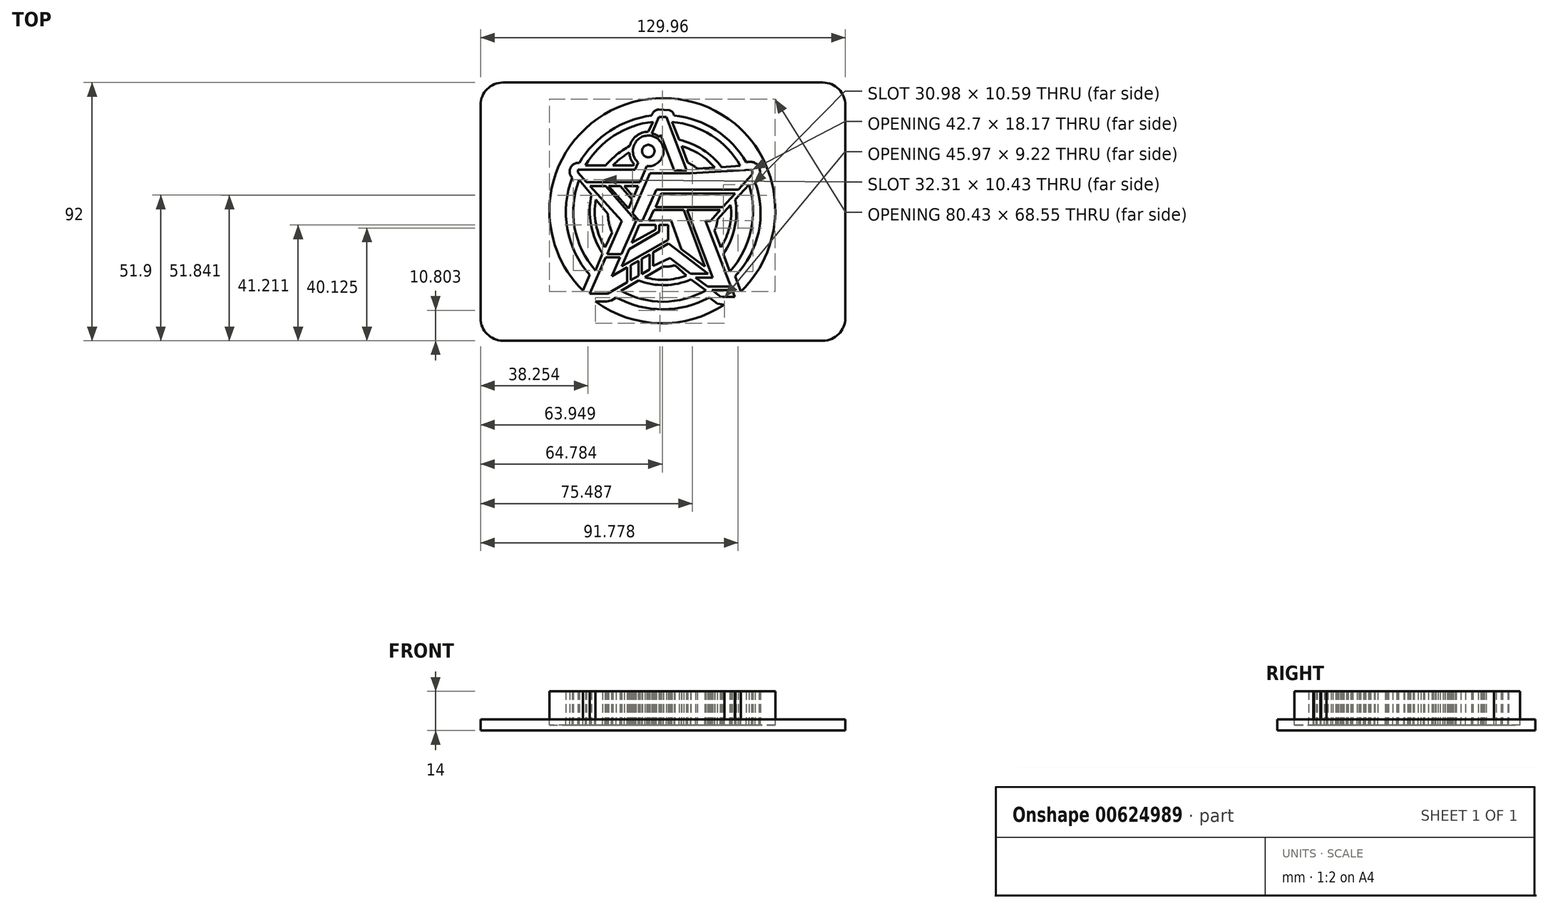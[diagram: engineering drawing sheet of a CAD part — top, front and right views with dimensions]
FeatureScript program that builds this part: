
annotation { "Feature Type Name" : "Feature", "Feature Type Description" : "" }
export const myFeature = defineFeature(function(context is Context, id is Id, definition is map)
    precondition{}
    {
        {
            var Q0;
            Q0=qCreatedBy(makeId("Top.planeOp"),FACE);
            var sketch = newSketch(context, id + "F0", { "sketchPlane" : qUnion([Q0])});
            skCircle(sketch, "E0", {"center": v(0, 0) * mm, "radius": 19.62 * mm, "construction": true});
            skCircle(sketch, "E1", {"center": v(0, 0) * mm, "radius": 24.24 * mm, "construction": true});
            skCircle(sketch, "E2", {"center": v(0, 0) * mm, "radius": 34.5 * mm, "construction": true});
            skLineSegment(sketch, "E3", {"start": v(20.7, -30.4) * mm, "end": v(2.49, -16.49) * mm, "construction": true});
            skLineSegment(sketch, "E4", {"start": v(2.49, -16.49) * mm, "end": v(-19.72, -29.2) * mm, "construction": true});
            skLineSegment(sketch, "E5", {"start": v(2, -11.38) * mm, "end": v(-18.24, -22.97) * mm, "construction": true});
            skLineSegment(sketch, "E6", {"start": v(-18.24, -22.97) * mm, "end": v(-9.56, -3.39) * mm, "construction": true});
            skLineSegment(sketch, "E7", {"start": v(-5.7, 16.2) * mm, "end": v(-12.28, 1.1) * mm, "construction": true});
            skLineSegment(sketch, "E8", {"start": v(-25.9, 9.11) * mm, "end": v(-8.79, 9.11) * mm, "construction": true});
            skLineSegment(sketch, "E9", {"start": v(23.83, -21.37) * mm, "end": v(18.4, -6.8) * mm, "construction": true});
            skLineSegment(sketch, "E10", {"start": v(30.66, 9.62) * mm, "end": v(19.42, -2.8) * mm, "construction": true});
            skLineSegment(sketch, "E11", {"start": v(25.58, -30.36) * mm, "end": v(15.19, -3.34) * mm, "construction": true});
            skLineSegment(sketch, "E12", {"start": v(15.19, -3.34) * mm, "end": v(16.91, -3.34) * mm, "construction": true});
            skLineSegment(sketch, "E13", {"start": v(16.91, -3.34) * mm, "end": v(31.66, 13.12) * mm, "construction": true});
            skLineSegment(sketch, "E14", {"start": v(27.56, 16.32) * mm, "end": v(12.3, 15.29) * mm, "construction": true});
            skLineSegment(sketch, "E15", {"start": v(3.31, 32) * mm, "end": v(8.9, 17.49) * mm, "construction": true});
            skArc(sketch, "E16", {"start": v(12.3, 15.29) * mm, "mid": v(10.66, 16.48) * mm, "end": v(8.9, 17.49) * mm});
            skArc(sketch, "E17", {"start": v(18.46, 15.7) * mm, "mid": v(13.15, 20.41) * mm, "end": v(6.66, 23.3) * mm});
            skArc(sketch, "E18", {"start": v(20.95, 15.87) * mm, "mid": v(14.22, 22.1) * mm, "end": v(5.77, 25.62) * mm});
            skArc(sketch, "E19", {"start": v(27.56, 16.32) * mm, "mid": v(17.36, 27.13) * mm, "end": v(3.31, 32) * mm});
            skLineSegment(sketch, "E20", {"start": v(3.31, 32) * mm, "end": v(5.77, 25.62) * mm});
            skLineSegment(sketch, "E21", {"start": v(6.66, 23.3) * mm, "end": v(8.9, 17.49) * mm});
            skLineSegment(sketch, "E22", {"start": v(12.3, 15.29) * mm, "end": v(18.46, 15.7) * mm});
            skLineSegment(sketch, "E23", {"start": v(20.95, 15.87) * mm, "end": v(27.56, 16.32) * mm});
            skLineSegment(sketch, "E24", {"start": v(-3.92, 27.8) * mm, "end": v(-1.42, 33.75) * mm});
            skLineSegment(sketch, "E25", {"start": v(-1.42, 33.75) * mm, "end": v(1.17, 33.75) * mm});
            skLineSegment(sketch, "E26", {"start": v(1.17, 33.75) * mm, "end": v(8.52, 14.66) * mm});
            skLineSegment(sketch, "E27", {"start": v(8.52, 14.66) * mm, "end": v(4.02, 14.66) * mm});
            skLineSegment(sketch, "E28", {"start": v(4.02, 14.66) * mm, "end": v(-0.78, 27.44) * mm});
            skLineSegment(sketch, "E29", {"start": v(-0.78, 27.44) * mm, "end": v(-1.24, 26.58) * mm});
            skArc(sketch, "E30", {"start": v(-1.24, 26.58) * mm, "mid": v(-2.48, 27.41) * mm, "end": v(-3.92, 27.8) * mm});
            skCircle(sketch, "E31", {"center": v(-5.21, 21.6) * mm, "radius": 2.2 * mm});
            skLineSegment(sketch, "E32", {"start": v(-5.7, 16.2) * mm, "end": v(-8.16, 10.56) * mm});
            skLineSegment(sketch, "E33", {"start": v(-8.16, 10.56) * mm, "end": v(-27.23, 10.56) * mm});
            skLineSegment(sketch, "E34", {"start": v(-27.23, 10.56) * mm, "end": v(-30.3, 13.9) * mm});
            skLineSegment(sketch, "E35", {"start": v(-30.3, 13.9) * mm, "end": v(-30.3, 14.9) * mm});
            skLineSegment(sketch, "E36", {"start": v(-30.3, 14.9) * mm, "end": v(-9.9, 14.9) * mm});
            skLineSegment(sketch, "E37", {"start": v(-9.9, 14.9) * mm, "end": v(-8.78, 17.49) * mm});
            skArc(sketch, "E38", {"start": v(-5.7, 16.2) * mm, "mid": v(-3.11, 26.69) * mm, "end": v(-8.78, 17.49) * mm});
            skLineSegment(sketch, "E39", {"start": v(-10.79, 16.46) * mm, "end": v(-10.16, 16.79) * mm});
            skLineSegment(sketch, "E40", {"start": v(-10.79, 16.46) * mm, "end": v(-17.8, 16.46) * mm});
            skArc(sketch, "E41", {"start": v(-11.95, 21.09) * mm, "mid": v(-15.04, 18.99) * mm, "end": v(-17.8, 16.46) * mm});
            skArc(sketch, "E42", {"start": v(-11.95, 21.09) * mm, "mid": v(-11.44, 18.78) * mm, "end": v(-10.16, 16.79) * mm});
            skArc(sketch, "E43", {"start": v(-5.2, 28.49) * mm, "mid": v(-9.36, 27.06) * mm, "end": v(-11.83, 23.42) * mm});
            skLineSegment(sketch, "E44", {"start": v(-5.2, 28.49) * mm, "end": v(-3.52, 32.02) * mm});
            skLineSegment(sketch, "E45", {"start": v(-20.38, 16.47) * mm, "end": v(-27.54, 16.47) * mm});
            skArc(sketch, "E46", {"start": v(-3.52, 32.02) * mm, "mid": v(-17.38, 27.1) * mm, "end": v(-27.54, 16.47) * mm});
            skArc(sketch, "E47", {"start": v(-11.83, 23.42) * mm, "mid": v(-16.43, 20.34) * mm, "end": v(-20.38, 16.47) * mm});
            skLineSegment(sketch, "E48", {"start": v(-13.82, 9.11) * mm, "end": v(-10.5, 5.18) * mm});
            skLineSegment(sketch, "E49", {"start": v(-10.5, 5.18) * mm, "end": v(-8.79, 9.11) * mm});
            skLineSegment(sketch, "E50", {"start": v(-13.82, 9.11) * mm, "end": v(-8.79, 9.11) * mm});
            skLineSegment(sketch, "E51", {"start": v(-19.38, 9.11) * mm, "end": v(-15.15, 9.11) * mm});
            skLineSegment(sketch, "E52", {"start": v(-15.15, 9.11) * mm, "end": v(-10.91, 4.22) * mm});
            skLineSegment(sketch, "E53", {"start": v(-10.91, 4.22) * mm, "end": v(-12.28, 1.1) * mm});
            skLineSegment(sketch, "E54", {"start": v(-12.28, 1.1) * mm, "end": v(-19.38, 9.11) * mm});
            skLineSegment(sketch, "E55", {"start": v(-25.9, 9.11) * mm, "end": v(-20.34, 9.11) * mm});
            skLineSegment(sketch, "E56", {"start": v(-20.34, 9.11) * mm, "end": v(-9.56, -3.39) * mm});
            skLineSegment(sketch, "E57", {"start": v(-9.56, -3.39) * mm, "end": v(-14.76, -15.11) * mm});
            skLineSegment(sketch, "E58", {"start": v(-14.76, -15.11) * mm, "end": v(-19.82, -15.11) * mm});
            skLineSegment(sketch, "E59", {"start": v(-19.82, -15.11) * mm, "end": v(-14.62, -3.39) * mm});
            skLineSegment(sketch, "E60", {"start": v(-14.62, -3.39) * mm, "end": v(-25.9, 9.11) * mm});
            skLineSegment(sketch, "E61", {"start": v(-7.25, -3.18) * mm, "end": v(-8.54, -3.18) * mm});
            skLineSegment(sketch, "E62", {"start": v(-8.54, -3.18) * mm, "end": v(-10.84, -0.58) * mm});
            skLineSegment(sketch, "E63", {"start": v(-10.84, -0.58) * mm, "end": v(-4.63, 13.7) * mm});
            skLineSegment(sketch, "E64", {"start": v(-4.63, 13.7) * mm, "end": v(9.88, 13.7) * mm});
            skLineSegment(sketch, "E65", {"start": v(9.88, 13.7) * mm, "end": v(31.6, 14.98) * mm});
            skLineSegment(sketch, "E66", {"start": v(31.66, 13.12) * mm, "end": v(26.93, 7.84) * mm});
            skLineSegment(sketch, "E67", {"start": v(26.93, 7.84) * mm, "end": v(-2.35, 7.84) * mm});
            skLineSegment(sketch, "E68", {"start": v(-2.35, 7.84) * mm, "end": v(-7.25, -3.18) * mm});
            skArc(sketch, "E69", {"start": v(31.66, 13.12) * mm, "mid": v(31.86, 14.06) * mm, "end": v(31.6, 14.98) * mm});
            skLineSegment(sketch, "E70", {"start": v(25.68, 6.44) * mm, "end": v(21.3, 1.56) * mm});
            skLineSegment(sketch, "E71", {"start": v(21.3, 1.56) * mm, "end": v(-2.63, 1.56) * mm});
            skLineSegment(sketch, "E72", {"start": v(-0.54, 6.55) * mm, "end": v(-4.93, -3.25) * mm, "construction": true});
            skLineSegment(sketch, "E73", {"start": v(1.9, -4.77) * mm, "end": v(-8.37, -4.77) * mm, "construction": true});
            skLineSegment(sketch, "E74", {"start": v(-8.37, -4.77) * mm, "end": v(-14.63, -19.5) * mm, "construction": true});
            skLineSegment(sketch, "E75", {"start": v(-11.07, -11.11) * mm, "end": v(-2.59, -6.39) * mm});
            skLineSegment(sketch, "E76", {"start": v(-2.59, -6.39) * mm, "end": v(-2.59, -4.77) * mm});
            skLineSegment(sketch, "E77", {"start": v(-2.59, -4.77) * mm, "end": v(-8.37, -4.77) * mm});
            skLineSegment(sketch, "E78", {"start": v(-11.07, -11.11) * mm, "end": v(-8.37, -4.77) * mm});
            skLineSegment(sketch, "E79", {"start": v(-1.37, -4.77) * mm, "end": v(1.9, -4.77) * mm});
            skLineSegment(sketch, "E80", {"start": v(1.9, -10.12) * mm, "end": v(1.9, -4.77) * mm});
            skLineSegment(sketch, "E81", {"start": v(1.9, -10.12) * mm, "end": v(-14.63, -19.5) * mm});
            skLineSegment(sketch, "E82", {"start": v(-1.37, -4.77) * mm, "end": v(-1.37, -7.1) * mm});
            skLineSegment(sketch, "E83", {"start": v(-1.37, -7.1) * mm, "end": v(-12.03, -13.38) * mm});
            skLineSegment(sketch, "E84", {"start": v(-12.03, -13.38) * mm, "end": v(-14.63, -19.5) * mm});
            skLineSegment(sketch, "E85", {"start": v(20.38, 0.53) * mm, "end": v(-3.24, 0.53) * mm, "construction": true});
            skLineSegment(sketch, "E86", {"start": v(-3.24, 0.53) * mm, "end": v(7.4, 0.53) * mm});
            skLineSegment(sketch, "E87", {"start": v(7.4, 0.53) * mm, "end": v(14.97, -19.6) * mm});
            skLineSegment(sketch, "E88", {"start": v(14.97, -19.6) * mm, "end": v(6.62, -13.36) * mm});
            skLineSegment(sketch, "E89", {"start": v(6.62, -13.36) * mm, "end": v(2.87, -3.12) * mm});
            skLineSegment(sketch, "E90", {"start": v(2.87, -3.12) * mm, "end": v(-4.93, -3.25) * mm});
            skLineSegment(sketch, "E91", {"start": v(-4.93, -3.25) * mm, "end": v(-3.24, 0.53) * mm});
            skLineSegment(sketch, "E92", {"start": v(20.38, 0.53) * mm, "end": v(8.57, 0.53) * mm});
            skLineSegment(sketch, "E93", {"start": v(8.57, 0.53) * mm, "end": v(17.74, -23.52) * mm});
            skLineSegment(sketch, "E94", {"start": v(17.74, -23.52) * mm, "end": v(11.7, -23.52) * mm});
            skLineSegment(sketch, "E95", {"start": v(11.7, -23.52) * mm, "end": v(15.95, -26.77) * mm});
            skLineSegment(sketch, "E96", {"start": v(15.95, -26.77) * mm, "end": v(24.2, -26.77) * mm});
            skLineSegment(sketch, "E97", {"start": v(24.2, -26.77) * mm, "end": v(15.19, -3.34) * mm});
            skLineSegment(sketch, "E98", {"start": v(15.19, -3.34) * mm, "end": v(16.91, -3.34) * mm});
            skLineSegment(sketch, "E99", {"start": v(16.91, -3.34) * mm, "end": v(20.38, 0.53) * mm});
            skLineSegment(sketch, "E100", {"start": v(-2.63, 1.56) * mm, "end": v(-0.54, 6.55) * mm});
            skLineSegment(sketch, "E101", {"start": v(-0.54, 6.55) * mm, "end": v(25.68, 6.44) * mm});
            skArc(sketch, "E102", {"start": v(18.4, -6.8) * mm, "mid": v(19.1, -4.85) * mm, "end": v(19.42, -2.8) * mm});
            skArc(sketch, "E103", {"start": v(20.62, -12.74) * mm, "mid": v(23.74, -5.5) * mm, "end": v(24.12, 2.38) * mm});
            skArc(sketch, "E104", {"start": v(21.5, -15.12) * mm, "mid": v(25.55, -5.86) * mm, "end": v(25.8, 4.24) * mm});
            skArc(sketch, "E105", {"start": v(23.83, -21.37) * mm, "mid": v(31.37, -6.79) * mm, "end": v(30.66, 9.62) * mm});
            skLineSegment(sketch, "E106", {"start": v(30.66, 9.62) * mm, "end": v(25.8, 4.24) * mm});
            skLineSegment(sketch, "E107", {"start": v(24.12, 2.38) * mm, "end": v(19.42, -2.8) * mm});
            skLineSegment(sketch, "E108", {"start": v(18.4, -6.8) * mm, "end": v(20.62, -12.74) * mm});
            skLineSegment(sketch, "E109", {"start": v(21.5, -15.12) * mm, "end": v(23.83, -21.37) * mm});
            skLineSegment(sketch, "E110", {"start": v(17.52, -27.97) * mm, "end": v(24.66, -27.97) * mm});
            skLineSegment(sketch, "E111", {"start": v(24.66, -27.97) * mm, "end": v(25.58, -30.36) * mm});
            skLineSegment(sketch, "E112", {"start": v(25.58, -30.36) * mm, "end": v(20.7, -30.4) * mm});
            skLineSegment(sketch, "E113", {"start": v(20.7, -30.4) * mm, "end": v(17.52, -27.97) * mm});
            skArc(sketch, "E114", {"start": v(0, -19.62) * mm, "mid": v(2.16, -19.55) * mm, "end": v(4.29, -19.15) * mm});
            skArc(sketch, "E115", {"start": v(-6.43, -23.37) * mm, "mid": v(1, -24.3) * mm, "end": v(8.3, -22.77) * mm});
            skArc(sketch, "E116", {"start": v(-8.72, -24.58) * mm, "mid": v(0.68, -26.2) * mm, "end": v(10, -24.17) * mm});
            skArc(sketch, "E117", {"start": v(-14.96, -28.23) * mm, "mid": v(0.19, -32.12) * mm, "end": v(15.28, -28.06) * mm});
            skLineSegment(sketch, "E118", {"start": v(15.28, -28.06) * mm, "end": v(10, -24.17) * mm});
            skLineSegment(sketch, "E119", {"start": v(8.3, -22.77) * mm, "end": v(4.29, -19.15) * mm});
            skLineSegment(sketch, "E120", {"start": v(-6.43, -23.37) * mm, "end": v(0.1, -19.62) * mm});
            skLineSegment(sketch, "E121", {"start": v(-8.72, -24.58) * mm, "end": v(-14.96, -28.23) * mm});
            skLineSegment(sketch, "E122", {"start": v(-3.41, -19.32) * mm, "end": v(-3.41, -14.49) * mm});
            skLineSegment(sketch, "E123", {"start": v(-3.41, -14.49) * mm, "end": v(2, -11.38) * mm});
            skLineSegment(sketch, "E124", {"start": v(2, -11.38) * mm, "end": v(16.13, -22.15) * mm});
            skLineSegment(sketch, "E125", {"start": v(16.13, -22.15) * mm, "end": v(9.9, -22.15) * mm});
            skLineSegment(sketch, "E126", {"start": v(9.9, -22.15) * mm, "end": v(2.49, -16.49) * mm});
            skLineSegment(sketch, "E127", {"start": v(2.49, -16.49) * mm, "end": v(-3.41, -19.32) * mm});
            skLineSegment(sketch, "E128", {"start": v(-4.73, -15.24) * mm, "end": v(-4.73, -20.62) * mm});
            skLineSegment(sketch, "E129", {"start": v(-4.73, -20.62) * mm, "end": v(-7.57, -22.25) * mm});
            skLineSegment(sketch, "E130", {"start": v(-7.57, -22.25) * mm, "end": v(-7.57, -16.87) * mm});
            skLineSegment(sketch, "E131", {"start": v(-7.57, -16.87) * mm, "end": v(-4.73, -15.24) * mm});
            skLineSegment(sketch, "E132", {"start": v(-8.7, -17.5) * mm, "end": v(-8.7, -22.89) * mm});
            skLineSegment(sketch, "E133", {"start": v(-8.7, -22.89) * mm, "end": v(-11.42, -24.45) * mm});
            skLineSegment(sketch, "E134", {"start": v(-11.42, -24.45) * mm, "end": v(-11.42, -19.07) * mm});
            skLineSegment(sketch, "E135", {"start": v(-11.42, -19.07) * mm, "end": v(-8.7, -17.5) * mm});
            skLineSegment(sketch, "E136", {"start": v(-12.7, -19.8) * mm, "end": v(-12.7, -25.18) * mm});
            skLineSegment(sketch, "E137", {"start": v(-12.7, -25.18) * mm, "end": v(-19.72, -29.2) * mm});
            skLineSegment(sketch, "E138", {"start": v(-26.12, -29.2) * mm, "end": v(-20.34, -16.27) * mm});
            skLineSegment(sketch, "E139", {"start": v(-20.34, -16.27) * mm, "end": v(-15.27, -16.27) * mm});
            skLineSegment(sketch, "E140", {"start": v(-15.27, -16.27) * mm, "end": v(-18.24, -22.97) * mm});
            skLineSegment(sketch, "E141", {"start": v(-18.24, -22.97) * mm, "end": v(-12.7, -19.8) * mm});
            skLineSegment(sketch, "E142", {"start": v(-18.24, -7.23) * mm, "end": v(-24.08, -20.94) * mm, "construction": true});
            skLineSegment(sketch, "E143", {"start": v(-19.57, -0.83) * mm, "end": v(-29.85, 11.36) * mm, "construction": true});
            skArc(sketch, "E144", {"start": v(-19.57, -0.83) * mm, "mid": v(-19.18, -4.21) * mm, "end": v(-18.1, -7.44) * mm});
            skArc(sketch, "E145", {"start": v(-23.86, 4.26) * mm, "mid": v(-23.85, -4.56) * mm, "end": v(-20.6, -12.77) * mm});
            skArc(sketch, "E146", {"start": v(-25.4, 6.09) * mm, "mid": v(-25.63, -4.81) * mm, "end": v(-21.51, -14.9) * mm});
            skArc(sketch, "E147", {"start": v(-29.85, 11.36) * mm, "mid": v(-31.47, -5.6) * mm, "end": v(-24.08, -20.94) * mm});
            skLineSegment(sketch, "E148", {"start": v(-19.57, -0.83) * mm, "end": v(-23.86, 4.26) * mm});
            skLineSegment(sketch, "E149", {"start": v(-25.4, 6.09) * mm, "end": v(-29.85, 11.36) * mm});
            skLineSegment(sketch, "E150", {"start": v(-18.1, -7.44) * mm, "end": v(-20.6, -12.77) * mm});
            skLineSegment(sketch, "E151", {"start": v(-21.51, -14.9) * mm, "end": v(-24.08, -20.94) * mm});
            skPoint(sketch, "E152.endSnap0", {"position": v(-25.63, -4.81) * mm});
            skArc(sketch, "E153", {"start": v(25.72, -23) * mm, "mid": v(34.06, -7.35) * mm, "end": v(32.92, 10.35) * mm});
            skArc(sketch, "E154", {"start": v(29.71, 17.55) * mm, "mid": v(18.86, 29.01) * mm, "end": v(3.98, 34.28) * mm});
            skArc(sketch, "E155", {"start": v(-3.98, 34.28) * mm, "mid": v(-18.86, 28.81) * mm, "end": v(-29.82, 17.37) * mm});
            skArc(sketch, "E156", {"start": v(-29.82, 17.37) * mm, "mid": v(-32.94, 15.64) * mm, "end": v(-32.3, 12.14) * mm});
            skArc(sketch, "E157", {"start": v(-1.42, 36.44) * mm, "mid": v(-3.07, 35.8) * mm, "end": v(-3.98, 34.28) * mm});
            skArc(sketch, "E158", {"start": v(3.98, 34.28) * mm, "mid": v(3.36, 35.48) * mm, "end": v(2.22, 36.2) * mm});
            skLineSegment(sketch, "E159", {"start": v(2.22, 36.2) * mm, "end": v(-1.42, 36.44) * mm});
            skArc(sketch, "E160", {"start": v(34.3, 15.87) * mm, "mid": v(32.32, 17.57) * mm, "end": v(29.71, 17.55) * mm});
            skArc(sketch, "E161", {"start": v(32.92, 10.35) * mm, "mid": v(34.45, 12.9) * mm, "end": v(34.3, 15.87) * mm});
            skLineSegment(sketch, "E162", {"start": v(25.72, -23) * mm, "end": v(27.79, -28.43) * mm});
            skLineSegment(sketch, "E163", {"start": v(19.4, -32.85) * mm, "end": v(21.95, -33.13) * mm});
            skLineSegment(sketch, "E164", {"start": v(-18.36, -31.69) * mm, "end": v(-20.07, -32.03) * mm});
            skLineSegment(sketch, "E165", {"start": v(-20.07, -32.03) * mm, "end": v(-24.02, -32.03) * mm});
            skArc(sketch, "E166", {"start": v(-32.3, 12.14) * mm, "mid": v(-34.03, -6.06) * mm, "end": v(-26.13, -22.54) * mm});
            skLineSegment(sketch, "E167", {"start": v(-26.13, -22.54) * mm, "end": v(-28.48, -28.16) * mm});
            skArc(sketch, "E168", {"start": v(27.79, -28.43) * mm, "mid": v(0, 40.74) * mm, "end": v(-28.48, -28.16) * mm});
            skArc(sketch, "E169", {"start": v(-16.63, -30.59) * mm, "mid": v(-0.02, -34.84) * mm, "end": v(16.59, -30.6) * mm});
            skLineSegment(sketch, "E170", {"start": v(19.4, -32.85) * mm, "end": v(16.59, -30.6) * mm});
            skLineSegment(sketch, "E171", {"start": v(-18.36, -31.69) * mm, "end": v(-16.63, -30.59) * mm});
            skArc(sketch, "E172", {"start": v(-24.02, -32.03) * mm, "mid": v(-1.2, -39.8) * mm, "end": v(21.95, -33.13) * mm});
            skCircle(sketch, "E173", {"center": v(0.01, -0.03) * mm, "radius": 40.5 * mm});
            skCircle(sketch, "E174", {"center": v(0.01, -0.03) * mm, "radius": 41.57 * mm});
            skLineSegment(sketch, "E175", {"start": v(-19.72, -29.2) * mm, "end": v(-26.12, -29.2) * mm});
            skSolve(sketch);
        }
        {
            var Q0;
            Q0=qCreatedBy(makeId("Top.planeOp"),FACE);
            var sketch = newSketch(context, id + "F1", { "sketchPlane" : qUnion([Q0])});
            skLineSegment(sketch, "E176.bottom", {"start": v(64.98, -46) * mm, "end": v(-64.98, -46) * mm});
            skLineSegment(sketch, "E176.top", {"start": v(64.98, 46) * mm, "end": v(-64.98, 46) * mm});
            skLineSegment(sketch, "E176.left", {"start": v(64.98, -46) * mm, "end": v(64.98, 46) * mm});
            skLineSegment(sketch, "E176.right", {"start": v(-64.98, -46) * mm, "end": v(-64.98, 46) * mm});
            skPoint(sketch, "E176.middle", {"position": v(0, 0) * mm});
            skSolve(sketch);
        }
        {
            var Q0;
            Q0 = qSketchRegion(id + "F1", true);
            extrude(context, id + "F2", {"entities" : qUnion([Q0]), "oppositeDirection" : true, "depth" : 4 * mm, "offsetDistance" : 25 * mm});
        }
        {
            var Q0;
            Q0=makeQuery(id+"F0.imprint","IMPRINT",FACE,{"disambiguationData":[TD([[makeQuery(id+"F0.imprint","IMPRINT",EDGE,{"derivedFrom":sQuery(id+"F0.wireOp",EDGE,"E153")}),-1.0]])]});
            var Q1;
            Q1=makeQuery(id+"F0.imprint","IMPRINT",FACE,{"disambiguationData":[TD([[makeQuery(id+"F0.imprint","IMPRINT",EDGE,{"derivedFrom":sQuery(id+"F0.wireOp",EDGE,"E24")}),-1.0]])]});
            var Q2;
            Q2=makeQuery(id+"F0.imprint","IMPRINT",FACE,{"disambiguationData":[TD([[makeQuery(id+"F0.imprint","IMPRINT",EDGE,{"derivedFrom":sQuery(id+"F0.wireOp",EDGE,"E31")}),-1.0]])]});
            var Q3;
            Q3=makeQuery(id+"F0.imprint","IMPRINT",FACE,{"disambiguationData":[TD([[makeQuery(id+"F0.imprint","IMPRINT",EDGE,{"derivedFrom":sQuery(id+"F0.wireOp",EDGE,"E18")}),-1.0]])]});
            var Q4;
            Q4=makeQuery(id+"F0.imprint","IMPRINT",FACE,{"disambiguationData":[TD([[makeQuery(id+"F0.imprint","IMPRINT",EDGE,{"derivedFrom":sQuery(id+"F0.wireOp",EDGE,"E16")}),-1.0]])]});
            var Q5;
            Q5=makeQuery(id+"F0.imprint","IMPRINT",FACE,{"disambiguationData":[TD([[makeQuery(id+"F0.imprint","IMPRINT",EDGE,{"derivedFrom":sQuery(id+"F0.wireOp",EDGE,"E43")}),-1.0]])]});
            var Q6;
            Q6=makeQuery(id+"F0.imprint","IMPRINT",FACE,{"disambiguationData":[TD([[makeQuery(id+"F0.imprint","IMPRINT",EDGE,{"derivedFrom":sQuery(id+"F0.wireOp",EDGE,"E39")}),1.0]])]});
            var Q7;
            Q7=makeQuery(id+"F0.imprint","IMPRINT",FACE,{"disambiguationData":[TD([[makeQuery(id+"F0.imprint","IMPRINT",EDGE,{"derivedFrom":sQuery(id+"F0.wireOp",EDGE,"E61")}),-1.0]])]});
            var Q8;
            Q8=makeQuery(id+"F0.imprint","IMPRINT",FACE,{"disambiguationData":[TD([[makeQuery(id+"F0.imprint","IMPRINT",EDGE,{"derivedFrom":sQuery(id+"F0.wireOp",EDGE,"E48")}),1.0]])]});
            var Q9;
            Q9=makeQuery(id+"F0.imprint","IMPRINT",FACE,{"disambiguationData":[TD([[makeQuery(id+"F0.imprint","IMPRINT",EDGE,{"derivedFrom":sQuery(id+"F0.wireOp",EDGE,"E51")}),-1.0]])]});
            var Q10;
            Q10=makeQuery(id+"F0.imprint","IMPRINT",FACE,{"disambiguationData":[TD([[makeQuery(id+"F0.imprint","IMPRINT",EDGE,{"derivedFrom":sQuery(id+"F0.wireOp",EDGE,"E70")}),-1.0]])]});
            var Q11;
            Q11=makeQuery(id+"F0.imprint","IMPRINT",FACE,{"disambiguationData":[TD([[makeQuery(id+"F0.imprint","IMPRINT",EDGE,{"derivedFrom":sQuery(id+"F0.wireOp",EDGE,"E86")}),-1.0]])]});
            var Q12;
            Q12=makeQuery(id+"F0.imprint","IMPRINT",FACE,{"disambiguationData":[TD([[makeQuery(id+"F0.imprint","IMPRINT",EDGE,{"derivedFrom":sQuery(id+"F0.wireOp",EDGE,"E92")}),1.0]])]});
            var Q13;
            Q13=makeQuery(id+"F0.imprint","IMPRINT",FACE,{"disambiguationData":[TD([[makeQuery(id+"F0.imprint","IMPRINT",EDGE,{"derivedFrom":sQuery(id+"F0.wireOp",EDGE,"E104")}),-1.0]])]});
            var Q14;
            Q14=makeQuery(id+"F0.imprint","IMPRINT",FACE,{"disambiguationData":[TD([[makeQuery(id+"F0.imprint","IMPRINT",EDGE,{"derivedFrom":sQuery(id+"F0.wireOp",EDGE,"E102")}),-1.0]])]});
            var Q15;
            Q15=makeQuery(id+"F0.imprint","IMPRINT",FACE,{"disambiguationData":[TD([[makeQuery(id+"F0.imprint","IMPRINT",EDGE,{"derivedFrom":sQuery(id+"F0.wireOp",EDGE,"E122")}),-1.0]])]});
            var Q16;
            Q16=makeQuery(id+"F0.imprint","IMPRINT",FACE,{"disambiguationData":[TD([[makeQuery(id+"F0.imprint","IMPRINT",EDGE,{"derivedFrom":sQuery(id+"F0.wireOp",EDGE,"E75")}),1.0]])]});
            var Q17;
            Q17=makeQuery(id+"F0.imprint","IMPRINT",FACE,{"disambiguationData":[TD([[makeQuery(id+"F0.imprint","IMPRINT",EDGE,{"derivedFrom":sQuery(id+"F0.wireOp",EDGE,"E79")}),-1.0]])]});
            var Q18;
            Q18=makeQuery(id+"F0.imprint","IMPRINT",FACE,{"disambiguationData":[TD([[makeQuery(id+"F0.imprint","IMPRINT",EDGE,{"derivedFrom":sQuery(id+"F0.wireOp",EDGE,"E55")}),-1.0]])]});
            var Q19;
            Q19=makeQuery(id+"F0.imprint","IMPRINT",FACE,{"disambiguationData":[TD([[makeQuery(id+"F0.imprint","IMPRINT",EDGE,{"derivedFrom":sQuery(id+"F0.wireOp",EDGE,"E128")}),-1.0]])]});
            var Q20;
            {var subQ4=sQuery(id+"F0.wireOp",EDGE,"E115");Q20=makeQuery(id+"F0.imprint","IMPRINT",FACE,{"disambiguationData":[TD([[makeQuery(id+"F0.imprint","IMPRINT",EDGE,{"derivedFrom":subQ4}),1.0]])]});}
            var Q21;
            Q21=makeQuery(id+"F0.imprint","IMPRINT",FACE,{"disambiguationData":[TD([[makeQuery(id+"F0.imprint","IMPRINT",EDGE,{"derivedFrom":sQuery(id+"F0.wireOp",EDGE,"E116")}),-1.0]])]});
            var Q22;
            Q22=makeQuery(id+"F0.imprint","IMPRINT",FACE,{"disambiguationData":[TD([[makeQuery(id+"F0.imprint","IMPRINT",EDGE,{"derivedFrom":sQuery(id+"F0.wireOp",EDGE,"E163")}),-1.0]])]});
            var Q23;
            Q23=makeQuery(id+"F0.imprint","IMPRINT",FACE,{"disambiguationData":[TD([[makeQuery(id+"F0.imprint","IMPRINT",EDGE,{"derivedFrom":sQuery(id+"F0.wireOp",EDGE,"E144")}),-1.0]])]});
            var Q24;
            Q24=makeQuery(id+"F0.imprint","IMPRINT",FACE,{"disambiguationData":[TD([[makeQuery(id+"F0.imprint","IMPRINT",EDGE,{"derivedFrom":sQuery(id+"F0.wireOp",EDGE,"E146")}),-1.0]])]});
            var Q25;
            Q25=makeQuery(id+"F0.imprint","IMPRINT",FACE,{"disambiguationData":[TD([[makeQuery(id+"F0.imprint","IMPRINT",EDGE,{"derivedFrom":sQuery(id+"F0.wireOp",EDGE,"E136")}),-1.0]])]});
            var Q26;
            Q26=makeQuery(id+"F0.imprint","IMPRINT",FACE,{"disambiguationData":[TD([[makeQuery(id+"F0.imprint","IMPRINT",EDGE,{"derivedFrom":sQuery(id+"F0.wireOp",EDGE,"E132")}),-1.0]])]});
            var Q27;
            Q27=makeQuery(id+"F0.imprint","IMPRINT",FACE,{"disambiguationData":[TD([[makeQuery(id+"F0.imprint","IMPRINT",EDGE,{"derivedFrom":sQuery(id+"F0.wireOp",EDGE,"E110")}),-1.0]])]});
            extrude(context, id + "F3", {"entities" : qUnion([Q0, Q1, Q2, Q3, Q4, Q5, Q6, Q7, Q8, Q9, Q10, Q11, Q12, Q13, Q14, Q15, Q16, Q17, Q18, Q19, Q20, Q21, Q22, Q23, Q24, Q25, Q26, Q27]), "operationType" : NewBodyOperationType.REMOVE, "oppositeDirection" : true, "depth" : 2 * mm, "offsetDistance" : 25 * mm});
        }
        {
            var Q0;
            Q0=makeQuery(id+"F2.opExtrude","SWEPT_EDGE",EDGE,{"disambiguationData":[OSD([sQuery(id+"F1.wireOp",EDGE,"E176.top"),sQuery(id+"F1.wireOp",EDGE,"E176.left")])]});
            var Q1;
            Q1=makeQuery(id+"F2.opExtrude","SWEPT_EDGE",EDGE,{"disambiguationData":[OSD([sQuery(id+"F1.wireOp",EDGE,"E176.top"),sQuery(id+"F1.wireOp",EDGE,"E176.right")])]});
            var Q2;
            Q2=makeQuery(id+"F2.opExtrude","SWEPT_EDGE",EDGE,{"disambiguationData":[OSD([sQuery(id+"F1.wireOp",EDGE,"E176.bottom"),sQuery(id+"F1.wireOp",EDGE,"E176.right")])]});
            var Q3;
            Q3=makeQuery(id+"F2.opExtrude","SWEPT_EDGE",EDGE,{"disambiguationData":[OSD([sQuery(id+"F1.wireOp",EDGE,"E176.bottom"),sQuery(id+"F1.wireOp",EDGE,"E176.left")])]});
            fillet(context, id + "F4", {"entities" : qUnion([Q0, Q1, Q2, Q3]), "radius" : 8 * mm, "tangentPropagation" : true, "allowEdgeOverflow" : false});
        }
        {
            var Q0;
            Q0=makeQuery(id+"F0.imprint","IMPRINT",FACE,{"disambiguationData":[TD([[makeQuery(id+"F0.imprint","IMPRINT",EDGE,{"derivedFrom":sQuery(id+"F0.wireOp",EDGE,"E31")}),-1.0]])]});
            var Q1;
            Q1=makeQuery(id+"F0.imprint","IMPRINT",FACE,{"disambiguationData":[TD([[makeQuery(id+"F0.imprint","IMPRINT",EDGE,{"derivedFrom":sQuery(id+"F0.wireOp",EDGE,"E39")}),1.0]])]});
            var Q2;
            Q2=makeQuery(id+"F0.imprint","IMPRINT",FACE,{"disambiguationData":[TD([[makeQuery(id+"F0.imprint","IMPRINT",EDGE,{"derivedFrom":sQuery(id+"F0.wireOp",EDGE,"E43")}),-1.0]])]});
            var Q3;
            Q3=makeQuery(id+"F0.imprint","IMPRINT",FACE,{"disambiguationData":[TD([[makeQuery(id+"F0.imprint","IMPRINT",EDGE,{"derivedFrom":sQuery(id+"F0.wireOp",EDGE,"E24")}),-1.0]])]});
            var Q4;
            Q4=makeQuery(id+"F0.imprint","IMPRINT",FACE,{"disambiguationData":[TD([[makeQuery(id+"F0.imprint","IMPRINT",EDGE,{"derivedFrom":sQuery(id+"F0.wireOp",EDGE,"E18")}),-1.0]])]});
            var Q5;
            Q5=makeQuery(id+"F0.imprint","IMPRINT",FACE,{"disambiguationData":[TD([[makeQuery(id+"F0.imprint","IMPRINT",EDGE,{"derivedFrom":sQuery(id+"F0.wireOp",EDGE,"E16")}),-1.0]])]});
            var Q6;
            Q6=makeQuery(id+"F0.imprint","IMPRINT",FACE,{"disambiguationData":[TD([[makeQuery(id+"F0.imprint","IMPRINT",EDGE,{"derivedFrom":sQuery(id+"F0.wireOp",EDGE,"E61")}),-1.0]])]});
            var Q7;
            Q7=makeQuery(id+"F0.imprint","IMPRINT",FACE,{"disambiguationData":[TD([[makeQuery(id+"F0.imprint","IMPRINT",EDGE,{"derivedFrom":sQuery(id+"F0.wireOp",EDGE,"E70")}),-1.0]])]});
            var Q8;
            Q8=makeQuery(id+"F0.imprint","IMPRINT",FACE,{"disambiguationData":[TD([[makeQuery(id+"F0.imprint","IMPRINT",EDGE,{"derivedFrom":sQuery(id+"F0.wireOp",EDGE,"E48")}),1.0]])]});
            var Q9;
            Q9=makeQuery(id+"F0.imprint","IMPRINT",FACE,{"disambiguationData":[TD([[makeQuery(id+"F0.imprint","IMPRINT",EDGE,{"derivedFrom":sQuery(id+"F0.wireOp",EDGE,"E51")}),-1.0]])]});
            var Q10;
            Q10=makeQuery(id+"F0.imprint","IMPRINT",FACE,{"disambiguationData":[TD([[makeQuery(id+"F0.imprint","IMPRINT",EDGE,{"derivedFrom":sQuery(id+"F0.wireOp",EDGE,"E55")}),-1.0]])]});
            var Q11;
            Q11=makeQuery(id+"F0.imprint","IMPRINT",FACE,{"disambiguationData":[TD([[makeQuery(id+"F0.imprint","IMPRINT",EDGE,{"derivedFrom":sQuery(id+"F0.wireOp",EDGE,"E75")}),1.0]])]});
            var Q12;
            Q12=makeQuery(id+"F0.imprint","IMPRINT",FACE,{"disambiguationData":[TD([[makeQuery(id+"F0.imprint","IMPRINT",EDGE,{"derivedFrom":sQuery(id+"F0.wireOp",EDGE,"E79")}),-1.0]])]});
            var Q13;
            Q13=makeQuery(id+"F0.imprint","IMPRINT",FACE,{"disambiguationData":[TD([[makeQuery(id+"F0.imprint","IMPRINT",EDGE,{"derivedFrom":sQuery(id+"F0.wireOp",EDGE,"E86")}),-1.0]])]});
            var Q14;
            Q14=makeQuery(id+"F0.imprint","IMPRINT",FACE,{"disambiguationData":[TD([[makeQuery(id+"F0.imprint","IMPRINT",EDGE,{"derivedFrom":sQuery(id+"F0.wireOp",EDGE,"E92")}),1.0]])]});
            var Q15;
            Q15=makeQuery(id+"F0.imprint","IMPRINT",FACE,{"disambiguationData":[TD([[makeQuery(id+"F0.imprint","IMPRINT",EDGE,{"derivedFrom":sQuery(id+"F0.wireOp",EDGE,"E102")}),-1.0]])]});
            var Q16;
            Q16=makeQuery(id+"F0.imprint","IMPRINT",FACE,{"disambiguationData":[TD([[makeQuery(id+"F0.imprint","IMPRINT",EDGE,{"derivedFrom":sQuery(id+"F0.wireOp",EDGE,"E104")}),-1.0]])]});
            var Q17;
            Q17=makeQuery(id+"F0.imprint","IMPRINT",FACE,{"disambiguationData":[TD([[makeQuery(id+"F0.imprint","IMPRINT",EDGE,{"derivedFrom":sQuery(id+"F0.wireOp",EDGE,"E153")}),-1.0]])]});
            var Q18;
            Q18=makeQuery(id+"F0.imprint","IMPRINT",FACE,{"disambiguationData":[TD([[makeQuery(id+"F0.imprint","IMPRINT",EDGE,{"derivedFrom":sQuery(id+"F0.wireOp",EDGE,"E110")}),-1.0]])]});
            var Q19;
            Q19=makeQuery(id+"F0.imprint","IMPRINT",FACE,{"disambiguationData":[TD([[makeQuery(id+"F0.imprint","IMPRINT",EDGE,{"derivedFrom":sQuery(id+"F0.wireOp",EDGE,"E116")}),-1.0]])]});
            var Q20;
            Q20=makeQuery(id+"F0.imprint","IMPRINT",FACE,{"disambiguationData":[TD([[makeQuery(id+"F0.imprint","IMPRINT",EDGE,{"derivedFrom":sQuery(id+"F0.wireOp",EDGE,"E163")}),-1.0]])]});
            var Q21;
            {var subQ4=sQuery(id+"F0.wireOp",EDGE,"E115");Q21=makeQuery(id+"F0.imprint","IMPRINT",FACE,{"disambiguationData":[TD([[makeQuery(id+"F0.imprint","IMPRINT",EDGE,{"derivedFrom":subQ4}),1.0]])]});}
            var Q22;
            Q22=makeQuery(id+"F0.imprint","IMPRINT",FACE,{"disambiguationData":[TD([[makeQuery(id+"F0.imprint","IMPRINT",EDGE,{"derivedFrom":sQuery(id+"F0.wireOp",EDGE,"E122")}),-1.0]])]});
            var Q23;
            Q23=makeQuery(id+"F0.imprint","IMPRINT",FACE,{"disambiguationData":[TD([[makeQuery(id+"F0.imprint","IMPRINT",EDGE,{"derivedFrom":sQuery(id+"F0.wireOp",EDGE,"E128")}),-1.0]])]});
            var Q24;
            Q24=makeQuery(id+"F0.imprint","IMPRINT",FACE,{"disambiguationData":[TD([[makeQuery(id+"F0.imprint","IMPRINT",EDGE,{"derivedFrom":sQuery(id+"F0.wireOp",EDGE,"E132")}),-1.0]])]});
            var Q25;
            Q25=makeQuery(id+"F0.imprint","IMPRINT",FACE,{"disambiguationData":[TD([[makeQuery(id+"F0.imprint","IMPRINT",EDGE,{"derivedFrom":sQuery(id+"F0.wireOp",EDGE,"E144")}),-1.0]])]});
            var Q26;
            Q26=makeQuery(id+"F0.imprint","IMPRINT",FACE,{"disambiguationData":[TD([[makeQuery(id+"F0.imprint","IMPRINT",EDGE,{"derivedFrom":sQuery(id+"F0.wireOp",EDGE,"E146")}),-1.0]])]});
            var Q27;
            Q27=makeQuery(id+"F0.imprint","IMPRINT",FACE,{"disambiguationData":[TD([[makeQuery(id+"F0.imprint","IMPRINT",EDGE,{"derivedFrom":sQuery(id+"F0.wireOp",EDGE,"E136")}),-1.0]])]});
            extrude(context, id + "F5", {"entities" : qUnion([Q0, Q1, Q2, Q3, Q4, Q5, Q6, Q7, Q8, Q9, Q10, Q11, Q12, Q13, Q14, Q15, Q16, Q17, Q18, Q19, Q20, Q21, Q22, Q23, Q24, Q25, Q26, Q27]), "depth" : 10 * mm, "offsetDistance" : 25 * mm});
        }
    });
